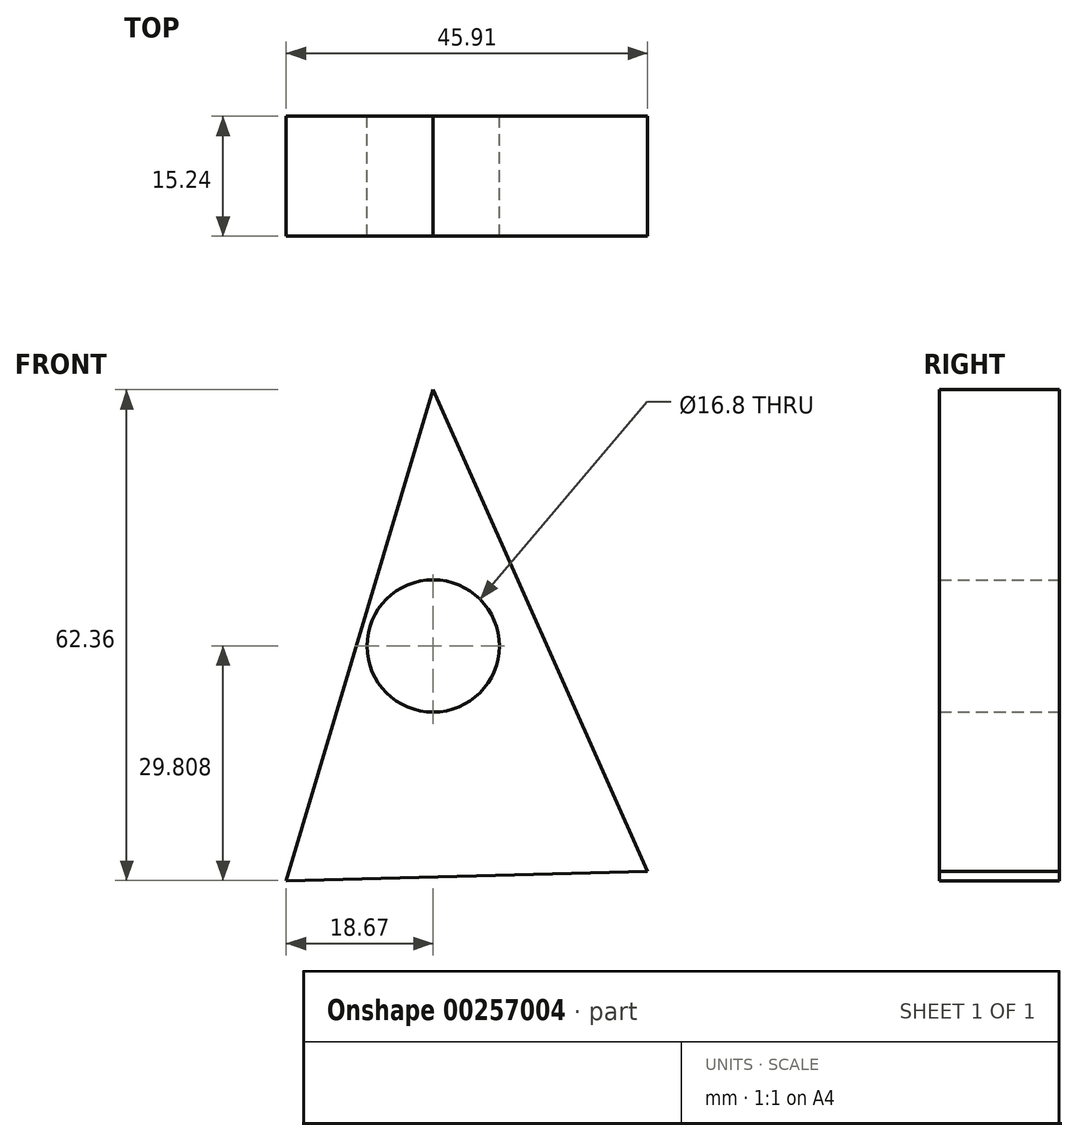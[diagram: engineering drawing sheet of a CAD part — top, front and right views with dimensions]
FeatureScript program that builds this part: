
annotation { "Feature Type Name" : "Feature", "Feature Type Description" : "" }
export const myFeature = defineFeature(function(context is Context, id is Id, definition is map)
    precondition{}
    {
        {
            var Q0;
            Q0=qCreatedBy(makeId("Front.planeOp"),FACE);
            var sketch = newSketch(context, id + "F0", { "sketchPlane" : qUnion([Q0])});
            skLineSegment(sketch, "E0", {"start": v(0, 41.29) * mm, "end": v(-18.67, -21.07) * mm});
            skLineSegment(sketch, "E1", {"start": v(0, 41.29) * mm, "end": v(27.24, -19.87) * mm});
            skLineSegment(sketch, "E2", {"start": v(-18.67, -21.07) * mm, "end": v(27.24, -19.87) * mm});
            skCircle(sketch, "E3", {"center": v(0, 8.74) * mm, "radius": 8.4 * mm});
            skSolve(sketch);
        }
        {
            var Q0;
            Q0=makeQuery(id+"F0.imprint","IMPRINT",FACE,{"disambiguationData":[TD([[makeQuery(id+"F0.imprint","IMPRINT",EDGE,{"derivedFrom":sQuery(id+"F0.wireOp",EDGE,"E0")}),1.0]])]});
            extrude(context, id + "F1", {"entities" : qUnion([Q0]), "depth" : 15.24 * mm});
        }
    });
